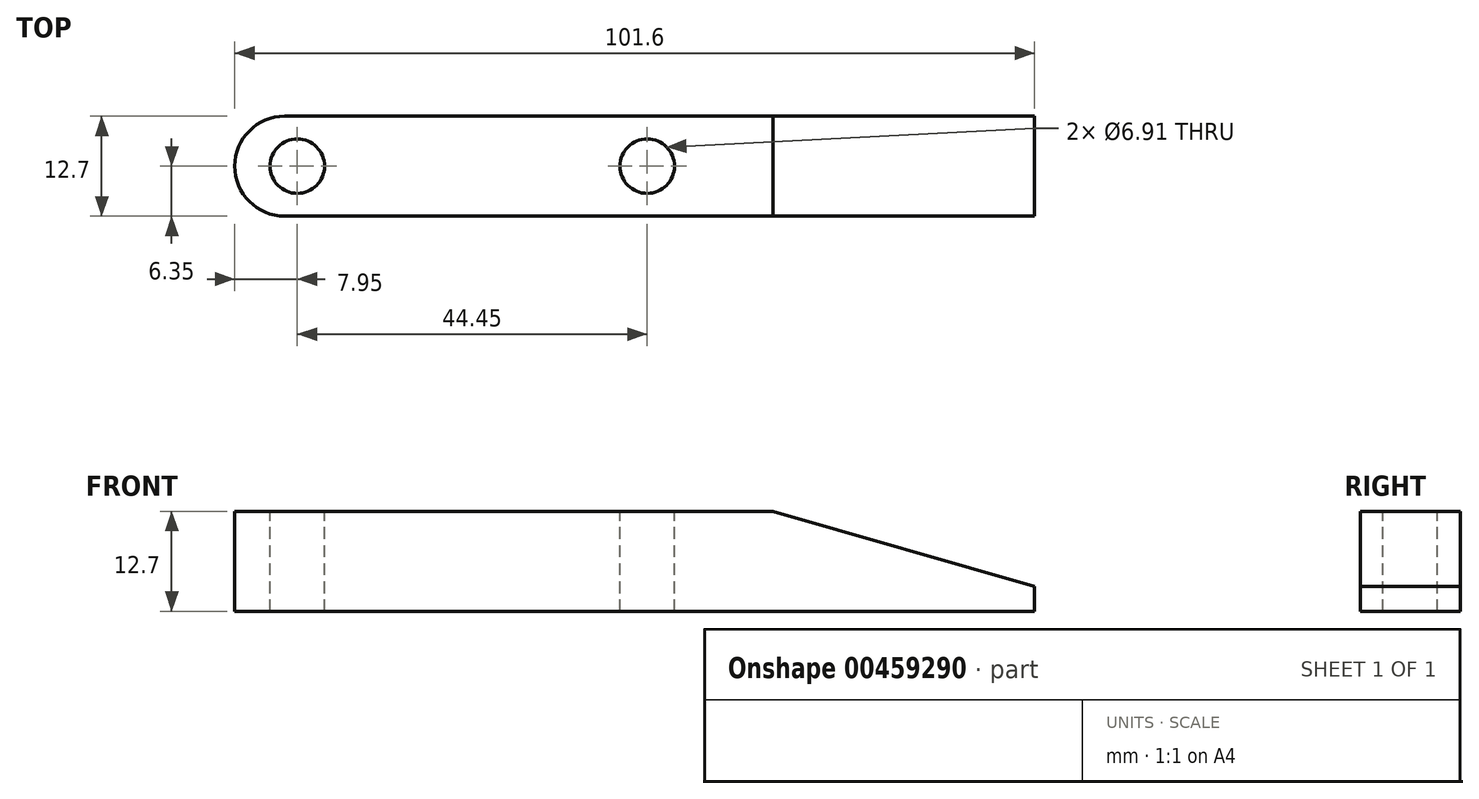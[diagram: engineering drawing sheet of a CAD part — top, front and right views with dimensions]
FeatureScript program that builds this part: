
annotation { "Feature Type Name" : "Feature", "Feature Type Description" : "" }
export const myFeature = defineFeature(function(context is Context, id is Id, definition is map)
    precondition{}
    {
        {
            var Q0;
            Q0=qCreatedBy(makeId("Front.planeOp"),FACE);
            var sketch = newSketch(context, id + "F0", { "sketchPlane" : qUnion([Q0])});
            skLineSegment(sketch, "E0", {"start": v(0, 0) * mm, "end": v(101.6, 0) * mm});
            skLineSegment(sketch, "E1", {"start": v(101.6, 0) * mm, "end": v(101.6, 3.18) * mm});
            skLineSegment(sketch, "E2", {"start": v(101.6, 3.17) * mm, "end": v(68.38, 12.7) * mm});
            skLineSegment(sketch, "E3", {"start": v(68.38, 12.7) * mm, "end": v(0, 12.7) * mm});
            skLineSegment(sketch, "E4", {"start": v(0, 12.7) * mm, "end": v(0, 0) * mm});
            skSolve(sketch);
        }
        {
            var Q0;
            Q0=makeQuery(id+"F0.imprint","IMPRINT",FACE,{"disambiguationData":[TD([[makeQuery(id+"F0.imprint","IMPRINT",EDGE,{"derivedFrom":sQuery(id+"F0.wireOp",EDGE,"E0")}),1.0]])]});
            extrude(context, id + "F1", {"entities" : qUnion([Q0]), "endBound" : BoundingType.SYMMETRIC, "depth" : 12.7 * mm});
        }
        {
            var Q0;
            Q0=makeQuery(id+"F1.opExtrude","SWEPT_FACE",FACE,{"disambiguationData":[OSD([sQuery(id+"F0.wireOp",EDGE,"E3")])]});
            var sketch = newSketch(context, id + "F2", { "sketchPlane" : qUnion([Q0])});
            skLineSegment(sketch, "E5", {"start": v(52.4, 24.27) * mm, "end": v(52.4, -26.02) * mm, "construction": true});
            skLineSegment(sketch, "E6", {"start": v(7.95, -23.26) * mm, "end": v(7.95, 24.87) * mm, "construction": true});
            skLineSegment(sketch, "E7", {"start": v(6.36, 23.68) * mm, "end": v(6.36, -26.61) * mm, "construction": true});
            skCircle(sketch, "E8", {"center": v(52.4, 0) * mm, "radius": 3.45 * mm});
            skCircle(sketch, "E9", {"center": v(7.95, 0) * mm, "radius": 3.45 * mm});
            skSolve(sketch);
        }
        {
            var Q0;
            Q0=makeQuery(id+"F1.opExtrude","CAP_EDGE",EDGE,{"disambiguationData":[OSD([sQuery(id+"F0.wireOp",EDGE,"E4")])],"isStart":false});
            var Q1;
            Q1=makeQuery(id+"F1.opExtrude","CAP_EDGE",EDGE,{"disambiguationData":[OSD([sQuery(id+"F0.wireOp",EDGE,"E4")])],"isStart":true});
            fillet(context, id + "F3", {"entities" : qUnion([Q0, Q1]), "radius" : 6.35 * mm, "tangentPropagation" : true, "allowEdgeOverflow" : false});
        }
        {
            var Q0;
            Q0=sQuery(id+"F2.wireOp",VERTEX,"E8.center");
            var Q1;
            Q1=sQuery(id+"F2.wireOp",VERTEX,"E9.center");
            var Q2;
            Q2=makeQuery(id+"F1.opExtrude","SWEPT_BODY",BODY,{"disambiguationData":[OSD([sQuery(id+"F0.wireOp",EDGE,"E0"),sQuery(id+"F0.wireOp",EDGE,"E1"),sQuery(id+"F0.wireOp",EDGE,"E2"),sQuery(id+"F0.wireOp",EDGE,"E3"),sQuery(id+"F0.wireOp",EDGE,"E4")])]});
            hole(context, id + "F4", {"style" : HoleStyle.SIMPLE, "endStyle" : HoleEndStyle.THROUGH, "standardTappedOrClearance" : lookupTablePath({ "standard" : "ANSI", "engagement" : "75%", "pitch" : "24 tpi", "size" : "5/16", "type" : "Tapped" }), "standardBlindInLast" : lookupTablePath({ "standard" : "ANSI", "engagement" : "75%", "pitch" : "24 tpi", "size" : "5/16", "type" : "Tapped" }), "holeDiameter" : 6.9 * mm, "showTappedDepth" : true, "isTappedThrough" : true, "tappedDepth" : 12.7 * mm, "tapClearance" : 3, "locations" : qUnion([Q0, Q1]), "scope" : qUnion([Q2]), "majorDiameter" : 7.94 * mm});
        }
    });
